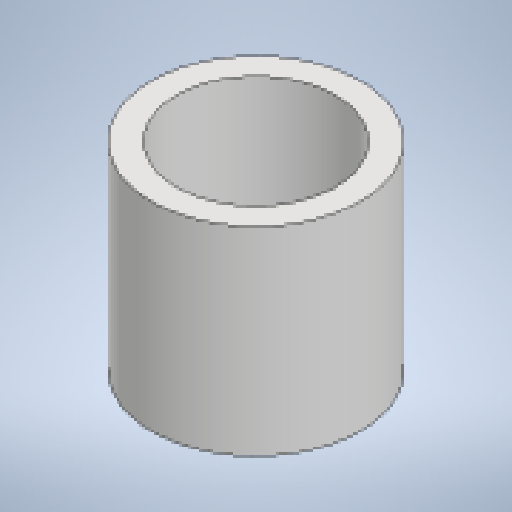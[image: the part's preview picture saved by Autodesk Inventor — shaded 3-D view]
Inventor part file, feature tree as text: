
AUTODESK INVENTOR PART (.ipt)
format: ipt  version: 2025.1 (Build 291241020, 241B)  size: 123,904 bytes
history: native  units: mm
features: extrude x1, sketch x1
ambient origin geometry x8: Origin, YZ Plane, XZ Plane, XY Plane, X Axis, Y Axis, Z Axis, Center Point
bodies: Solid1 (feature_tree)
feature tree (2):
  extrude  "Extrusion1"  Depth=20.0mm
  sketch  "Sketch1"  dims[d0=21.0mm d1=16.0mm d2=20.0mm d3=0.0mm]
